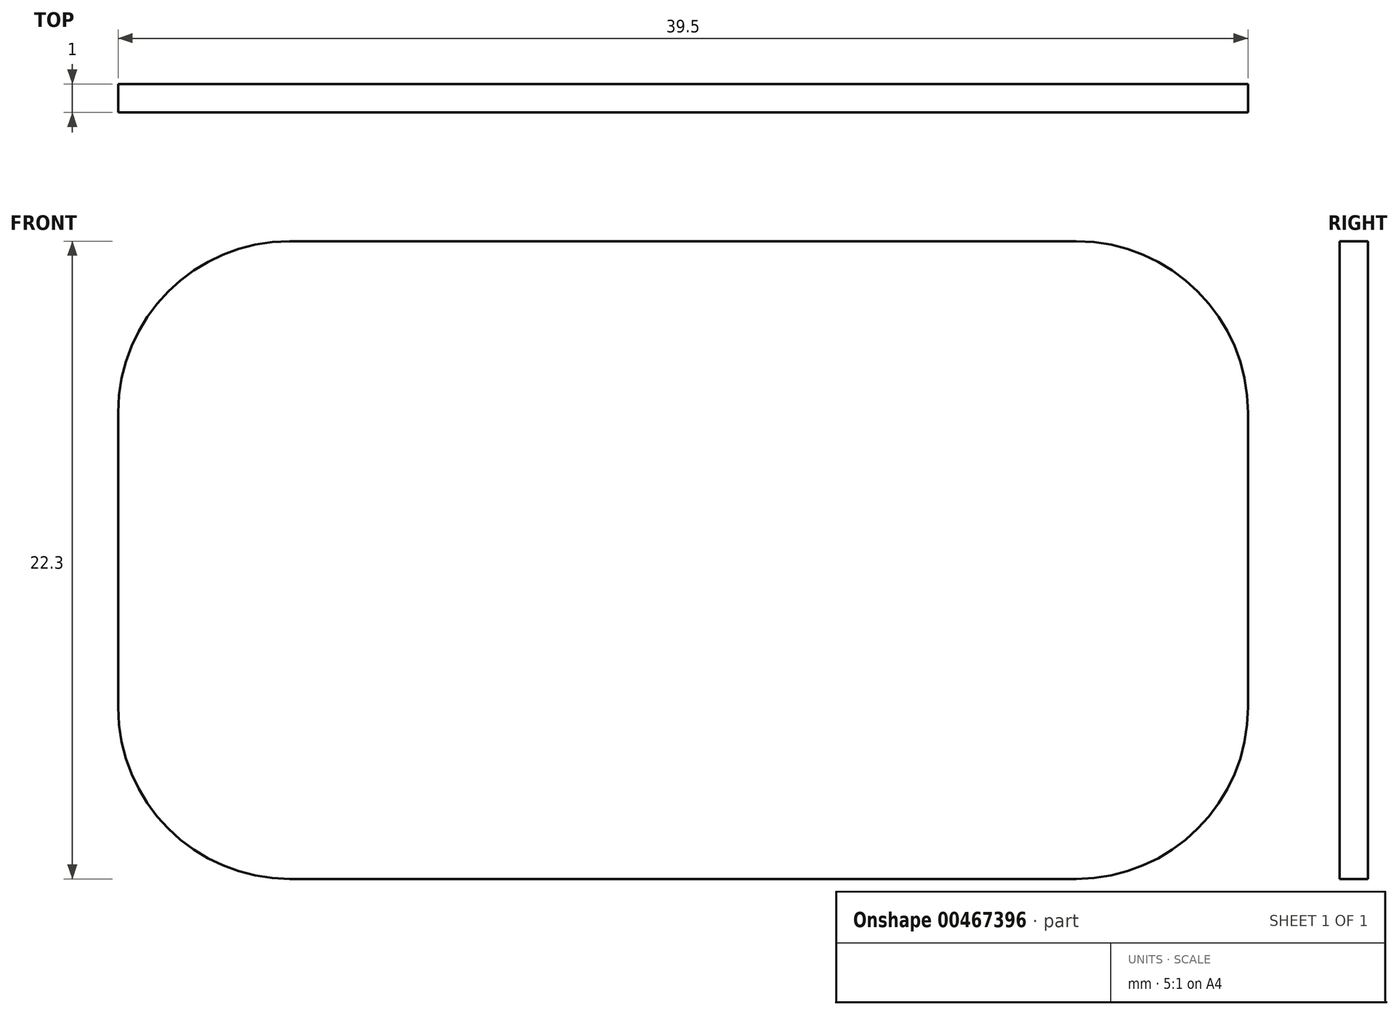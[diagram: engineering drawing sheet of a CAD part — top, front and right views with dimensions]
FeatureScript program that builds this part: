
annotation { "Feature Type Name" : "Feature", "Feature Type Description" : "" }
export const myFeature = defineFeature(function(context is Context, id is Id, definition is map)
    precondition{}
    {
        {
            var Q0;
            Q0=qCreatedBy(makeId("Front.planeOp"),FACE);
            var sketch = newSketch(context, id + "F0", { "sketchPlane" : qUnion([Q0])});
            skLineSegment(sketch, "E0.bottom", {"start": v(6, 0) * mm, "end": v(33.5, 0) * mm});
            skLineSegment(sketch, "E0.top", {"start": v(6, -22.3) * mm, "end": v(33.5, -22.3) * mm});
            skLineSegment(sketch, "E0.left", {"start": v(0, -6) * mm, "end": v(0, -16.3) * mm});
            skLineSegment(sketch, "E0.right", {"start": v(39.5, -6) * mm, "end": v(39.5, -16.3) * mm});
            skPoint(sketch, "E1.visualSharp", {"position": v(0, 0) * mm});
            skArc(sketch, "E1.filletArc", {"start": v(6, 0) * mm, "mid": v(1.76, -1.76) * mm, "end": v(0, -6) * mm});
            skPoint(sketch, "E2.visualSharp", {"position": v(0, -22.3) * mm});
            skArc(sketch, "E2.filletArc", {"start": v(0, -16.3) * mm, "mid": v(1.76, -20.54) * mm, "end": v(6, -22.3) * mm});
            skPoint(sketch, "E3.visualSharp", {"position": v(39.5, -22.3) * mm});
            skArc(sketch, "E3.filletArc", {"start": v(33.5, -22.3) * mm, "mid": v(37.74, -20.54) * mm, "end": v(39.5, -16.3) * mm});
            skPoint(sketch, "E4.visualSharp", {"position": v(39.5, 0) * mm});
            skArc(sketch, "E4.filletArc", {"start": v(39.5, -6) * mm, "mid": v(37.74, -1.76) * mm, "end": v(33.5, 0) * mm});
            skSolve(sketch);
        }
        {
            var Q0;
            Q0=makeQuery(id+"F0.imprint","IMPRINT",FACE,{"disambiguationData":[TD([[makeQuery(id+"F0.imprint","IMPRINT",EDGE,{"derivedFrom":sQuery(id+"F0.wireOp",EDGE,"E0.bottom")}),-1.0]])]});
            extrude(context, id + "F1", {"entities" : qUnion([Q0]), "depth" : 1 * mm, "offsetDistance" : 25 * mm});
        }
    });
